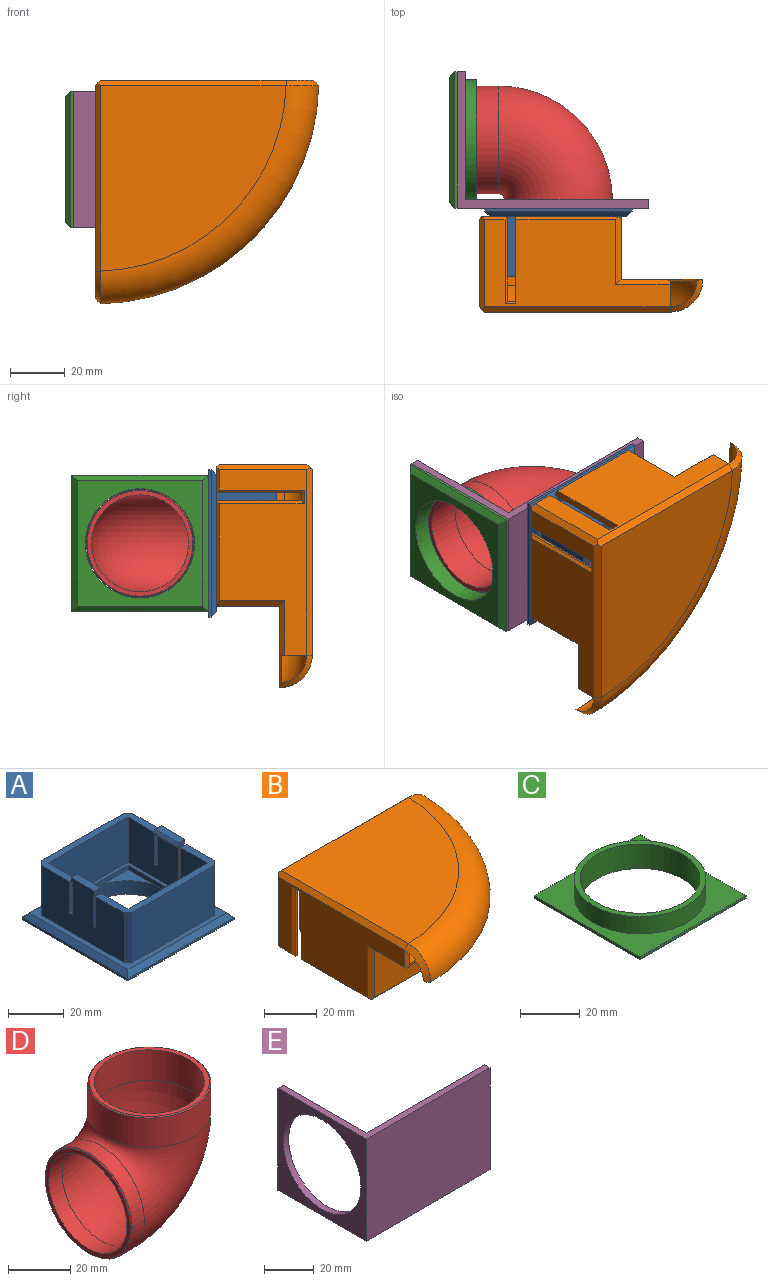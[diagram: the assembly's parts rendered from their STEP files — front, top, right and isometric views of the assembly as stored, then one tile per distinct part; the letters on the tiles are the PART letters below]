
ASSEMBLY  parts=5 mates=4
PART A: 68 faces, bbox 54x54x30 mm
  f0: cylinder r=22mm len=44mm, axis (0,0,1), area 414.7mm2, adj f53,f55
  f1: plane 12.49x1mm, normal (0,0,-1), area 8.4mm2, adj f16,f52
  f2: plane 12.49x1mm, normal (0,0,-1), area 8.4mm2, adj f15,f52
  f3: plane 12.49x1mm, normal (0,0,-1), area 8.4mm2, adj f18,f52
  f4: plane 12.49x1mm, normal (0,0,-1), area 8.4mm2, adj f17,f52
  f5: plane 40.5x20.5mm, normal (1,0,0), area 782.4mm2, adj f8,f9,f13,f14,f19,f20,f21,f34
  f6: plane 40.5x20.5mm, normal (-1,0,0), area 782.4mm2, adj f8,f9,f13,f14,f19,f23,f24,f26
  f7: plane 42x24mm, normal (1,0,0), area 914.4mm2, adj f8,f9,f23,f24,f25,f26,f27,f28
  f8: plane 46x16.4mm, normal (0,0,1), area 197.6mm2, adj f5,f6,f7,f11,f12,f14,f33,f34
  f9: plane 46x16.4mm, normal (0,0,1), area 197.6mm2, adj f5,f6,f7,f10,f11,f13,f29,f39
  f10: plane 42x22mm, normal (0,1,0), area 924mm2, adj f9,f54,f61,f62
  f11: plane 42x24mm, normal (-1,0,0), area 914.4mm2, adj f8,f9,f20,f21,f22,f34,f35,f36
  f12: plane 42x22mm, normal (0,-1,0), area 924mm2, adj f8,f54,f60,f63
  f13: plane 40.5x20mm, normal (0,-1,0), area 810mm2, adj f5,f6,f9,f19
  f14: plane 40.5x20mm, normal (0,1,0), area 810mm2, adj f5,f6,f8,f19
  f15: plane 38x2mm, normal (1,0,0), area 76mm2, adj f2,f16,f18,f19,f48,f49
  f16: plane 38x2mm, normal (0,-1,0), area 76mm2, adj f1,f15,f17,f19,f48,f50
  f17: plane 38x2mm, normal (-1,0,0), area 76mm2, adj f4,f16,f18,f19,f50,f51
  f18: plane 38x2mm, normal (0,1,0), area 76mm2, adj f3,f15,f17,f19,f49,f51
  f19: plane 40.5x40.5mm, normal (0,0,1), area 196.3mm2, adj f5,f6,f13,f14,f15,f16,f17,f18
  f20: plane 4.25x2mm, normal (0,-1,0), area 7.3mm2, adj f5,f11,f22,f35,f42,f43,f44
  f21: plane 4.25x2mm, normal (0,1,0), area 7.3mm2, adj f5,f11,f22,f38,f42,f43,f44
  f22: plane 12x3.25mm, normal (0,0,1), area 39mm2, adj f11,f20,f21,f44
  f23: plane 4.25x2mm, normal (0,-1,0), area 7.3mm2, adj f6,f7,f25,f30,f45,f46,f47
  f24: plane 4.25x2mm, normal (0,1,0), area 7.3mm2, adj f6,f7,f25,f26,f45,f46,f47
  f25: plane 12x3.25mm, normal (0,0,1), area 39mm2, adj f7,f23,f24,f47
  f26: plane 2.75x0.6mm, normal (0,0,-1), area 1.6mm2, adj f6,f7,f24,f27
  f27: plane 14x2.75mm, normal (0,1,0), area 38.5mm2, adj f6,f7,f26,f28
  f28: plane 2.75x1.2mm, normal (0,0,1), area 3.3mm2, adj f6,f7,f27,f29
  f29: plane 14x2.75mm, normal (0,-1,0), area 38.5mm2, adj f6,f7,f9,f28
  f30: plane 2.75x0.6mm, normal (0,0,-1), area 1.6mm2, adj f6,f7,f23,f32
  f31: plane 2.75x1.2mm, normal (0,0,1), area 3.3mm2, adj f6,f7,f32,f33
  f32: plane 14x2.75mm, normal (0,-1,0), area 38.5mm2, adj f6,f7,f30,f31
  f33: plane 14x2.75mm, normal (0,1,0), area 38.5mm2, adj f6,f7,f8,f31
  f34: plane 14x2.75mm, normal (0,1,0), area 38.5mm2, adj f5,f8,f11,f37
  f35: plane 2.75x0.6mm, normal (0,0,-1), area 1.7mm2, adj f5,f11,f20,f36
  f36: plane 14x2.75mm, normal (0,-1,0), area 38.5mm2, adj f5,f11,f35,f37
  f37: plane 2.75x1.2mm, normal (0,0,1), area 3.3mm2, adj f5,f11,f34,f36
  f38: plane 2.75x0.6mm, normal (0,0,-1), area 1.7mm2, adj f5,f11,f21,f41
  f39: plane 14x2.75mm, normal (0,-1,0), area 38.5mm2, adj f5,f9,f11,f40
  f40: plane 2.75x1.2mm, normal (0,0,1), area 3.3mm2, adj f5,f11,f39,f41
  f41: plane 14x2.75mm, normal (0,1,0), area 38.5mm2, adj f5,f11,f38,f40
  f42: plane 12x1.5mm, normal (0,0,-1), area 18mm2, adj f5,f20,f21,f43
  f43: plane 12x0.5mm, normal (1,0,0), area 6mm2, adj f20,f21,f42,f44
  f44: plane 12x1mm, normal (0.71,0,0.71), area 17mm2, adj f20,f21,f22,f43
  f45: plane 12x1.5mm, normal (0,0,-1), area 18mm2, adj f6,f23,f24,f46
  f46: plane 12x0.5mm, normal (-1,0,0), area 6mm2, adj f23,f24,f45,f47
  f47: plane 12x1mm, normal (-0.71,0,0.71), area 17mm2, adj f23,f24,f25,f46
  f48: plane 12.76x12.76mm, normal (0,0,1), area 55.2mm2, adj f15,f16,f52
  f49: plane 12.76x12.76mm, normal (0,0,1), area 55.2mm2, adj f15,f18,f52
  f50: plane 12.76x12.76mm, normal (0,0,1), area 55.2mm2, adj f16,f17,f52
  f51: plane 12.76x12.76mm, normal (0,0,1), area 55.2mm2, adj f17,f18,f52
  f52: cylinder r=20mm len=40mm, axis (0,0,1), area 754mm2, adj f1,f2,f3,f4,f48,f49,f50,f51
  f53: plane 44x44mm, normal (0,0,-1), area 263.9mm2, adj f0,f52
  f54: plane 50x50mm, normal (0,0,1), area 392mm2, adj f7,f10,f11,f12,f60,f61,f62,f63
  f55: plane 54x54mm, normal (0,0,-1), area 1395.5mm2, adj f0,f56,f57,f58,f59
  f56: plane 54x1mm, normal (0,1,0), area 54mm2, adj f55,f57,f59,f67
  f57: plane 54x1mm, normal (1,0,0), area 54mm2, adj f55,f56,f58,f66
  f58: plane 54x1mm, normal (0,-1,0), area 54mm2, adj f55,f57,f59,f64
  f59: plane 54x1mm, normal (-1,0,0), area 54mm2, adj f55,f56,f58,f65
  f60: plane 22x2mm, normal (-0.71,-0.71,0), area 62.2mm2, adj f8,f11,f12,f54
  f61: plane 22x2mm, normal (-0.71,0.71,0), area 62.2mm2, adj f9,f10,f11,f54
  f62: plane 22x2mm, normal (0.71,0.71,0), area 62.2mm2, adj f7,f9,f10,f54
  f63: plane 22x2mm, normal (0.71,-0.71,0), area 62.2mm2, adj f7,f8,f12,f54
  f64: plane 54x2mm, normal (0,-0.71,0.71), area 147.1mm2, adj f54,f58,f65,f66
  f65: plane 54x2mm, normal (-0.71,0,0.71), area 147.1mm2, adj f54,f59,f64,f67
  f66: plane 54x2mm, normal (0.71,0,0.71), area 147.1mm2, adj f54,f57,f64,f67
  f67: plane 54x2mm, normal (0,0.71,0.71), area 147.1mm2, adj f54,f56,f65,f66
PART B: 59 faces, bbox 88.7x88.7x35 mm
  f0: plane 65.2x33mm, normal (1,0,0), area 1424.1mm2, adj f1,f3,f11,f12,f16,f30,f33,f42
  f1: plane 50x50mm, normal (0,0,-1), area 302.6mm2, adj f0,f8,f9,f10,f31,f32,f33,f35
  f2: cylinder r=70mm len=46.86mm, axis (0,0,1), area 72.8mm2, adj f5,f6,f8,f11,f17,f29,f54
  f3: cylinder r=70mm len=46.86mm, axis (0,0,1), area 72.8mm2, adj f0,f4,f7,f11,f17,f28,f58
  f4: plane 48.01x24.01mm, normal (0,-1,0), area 1063mm2, adj f3,f11,f14,f20,f22,f57,f58
  f5: plane 48.01x24.01mm, normal (1,0,0), area 1063mm2, adj f2,f11,f13,f20,f21,f54,f56
  f6: plane 68x32mm, normal (0,1,0), area 1572mm2, adj f2,f21,f23,f26,f27,f29,f35,f45
  f7: plane 68x32mm, normal (-1,0,0), area 1541mm2, adj f3,f22,f23,f24,f25,f28,f48,f49
  f8: plane 65.2x33mm, normal (0,-1,0), area 1456.1mm2, adj f1,f2,f11,f12,f16,f30,f31,f35
  f9: plane 42.5x25mm, normal (-1,0,0), area 1062.5mm2, adj f1,f11,f31,f32
  f10: plane 42.5x25mm, normal (0,1,0), area 1062.5mm2, adj f1,f11,f32,f33
  f11: plane 67.2x67.2mm, normal (0,0,1), area 1325.6mm2, adj f0,f2,f3,f4,f5,f8,f9,f10
  f12: plane 9.5x9.5mm, normal (0,0,-1), area 31.2mm2, adj f0,f8,f30,f36,f39,f40,f43,f45
  f13: plane 43.35x16.97mm, normal (0,0,-1), area 494.2mm2, adj f5,f29,f54
  f14: plane 43.35x16.97mm, normal (0,0,-1), area 494.2mm2, adj f4,f28,f58
  f15: plane 67.97x67.97mm, normal (0,0,1), area 3572.3mm2, adj f19,f25,f26
  f16: plane 67.2x67.2mm, normal (0,0,-1), area 3469.1mm2, adj f0,f8,f17,f30
  f17: torus R=70mm, axis (0,0,-1), area 1769.5mm2, adj f2,f3,f16,f24,f27,f53
  f18: plane 80.98x80.98mm, normal (0,0,-1), area 130.5mm2, adj f19,f24,f27,f53
  f19: torus R=70mm, axis (0,0,-1), area 2220.5mm2, adj f15,f18,f24,f27
  f20: plane 25x2mm, normal (0.71,-0.71,0), area 69.3mm2, adj f4,f5,f11,f56,f57
  f21: plane 25x2mm, normal (0.71,0.71,0), area 66.5mm2, adj f5,f6,f29,f55,f56
  f22: plane 25x2mm, normal (-0.71,-0.71,0), area 66.5mm2, adj f4,f7,f28,f49,f57
  f23: plane 34x2mm, normal (-0.71,0.71,0), area 93.3mm2, adj f6,f7,f25,f26,f45,f48
  f24: bspline ~12x12mm, area 48.3mm2, adj f7,f17,f18,f19,f25,f53
  f25: plane 68.97x2mm, normal (-0.71,0,0.71), area 193.7mm2, adj f7,f15,f23,f24,f26
  f26: plane 68.97x2mm, normal (0,0.71,0.71), area 193.7mm2, adj f6,f15,f23,f25,f27
  f27: bspline ~12x12mm, area 48.3mm2, adj f6,f17,f18,f19,f26,f53
  f28: plane 20.01x2.01mm, normal (-0.71,0,-0.71), area 53mm2, adj f3,f7,f14,f22,f58
  f29: plane 20.01x2.01mm, normal (0,0.71,-0.71), area 53mm2, adj f2,f6,f13,f21,f54
  f30: plane 33x2mm, normal (0.71,-0.71,0), area 93.3mm2, adj f0,f8,f12,f16
  f31: plane 25x2mm, normal (-0.71,-0.71,0), area 70.7mm2, adj f1,f8,f9,f11
  f32: plane 25x2mm, normal (-0.71,0.71,0), area 70.7mm2, adj f1,f9,f10,f11
  f33: plane 25x2mm, normal (0.71,0.71,0), area 70.7mm2, adj f0,f1,f10,f11
  f34: plane 3x0.75mm, normal (0,0,-1), area 2.3mm2, adj f35,f36,f41,f47
  f35: plane 32x2.75mm, normal (-1,0,0), area 85.8mm2, adj f1,f6,f8,f34,f41,f47,f55
  f36: plane 31x0.75mm, normal (1,0,0), area 23.3mm2, adj f12,f34,f40,f46
  f37: plane 31x0.75mm, normal (0,1,0), area 23.3mm2, adj f1,f38,f42,f51
  f38: plane 3x0.75mm, normal (0,0,-1), area 2.3mm2, adj f37,f39,f44,f52
  f39: plane 31x0.75mm, normal (0,-1,0), area 23.3mm2, adj f12,f38,f43,f50
  f40: plane 32x1mm, normal (0.71,-0.71,0), area 44.5mm2, adj f8,f12,f36,f41
  f41: plane 4x1mm, normal (0,-0.71,-0.71), area 4.9mm2, adj f8,f34,f35,f40
  f42: plane 32x1mm, normal (0.71,0.71,0), area 44.5mm2, adj f0,f1,f37,f44
  f43: plane 32x1mm, normal (0.71,-0.71,0), area 44.5mm2, adj f0,f12,f39,f44
  f44: plane 5x1mm, normal (0.71,0,-0.71), area 5.7mm2, adj f0,f38,f42,f43
  f45: plane 9.5x1mm, normal (0,0.71,-0.71), area 12mm2, adj f6,f12,f23,f46
  f46: plane 32x1mm, normal (0.71,0.71,0), area 43.8mm2, adj f6,f36,f45,f47
  f47: plane 4x1mm, normal (0,0.71,-0.71), area 4.9mm2, adj f6,f34,f35,f46
  f48: plane 9.5x1mm, normal (-0.71,0,-0.71), area 12mm2, adj f7,f12,f23,f50
  f49: plane 37.5x1mm, normal (-0.71,0,-0.71), area 51.6mm2, adj f1,f7,f22,f51
  f50: plane 32x1mm, normal (-0.71,-0.71,0), area 43.8mm2, adj f7,f39,f48,f52
  f51: plane 32x1mm, normal (-0.71,0.71,0), area 43.8mm2, adj f7,f37,f49,f52
  f52: plane 5x1mm, normal (-0.71,0,-0.71), area 5.7mm2, adj f7,f38,f50,f51
  f53: cone r=79.96mm half-angle=47.6deg, axis (0,0,-1), area 169mm2, adj f17,f18,f24,f27
  f54: cone r=70mm half-angle=45deg, axis (0,0,1), area 69.2mm2, adj f2,f5,f13,f29
  f55: plane 37.5x1mm, normal (0,0.71,-0.71), area 52.3mm2, adj f1,f6,f21,f35
  f56: plane 50x1mm, normal (0.71,0,-0.71), area 69.3mm2, adj f1,f5,f20,f21
  f57: plane 50x1mm, normal (0,-0.71,-0.71), area 69.3mm2, adj f1,f4,f20,f22
  f58: cone r=70mm half-angle=45deg, axis (0,0,1), area 69.2mm2, adj f3,f4,f14,f28
PART C: 13 faces, bbox 50x50x10 mm
  f0: plane 50x1mm, normal (0,1,0), area 50mm2, adj f1,f3,f4,f12
  f1: plane 50x1mm, normal (-1,0,0), area 50mm2, adj f0,f2,f4,f10
  f2: plane 50x1mm, normal (0,-1,0), area 50mm2, adj f1,f3,f4,f9
  f3: plane 50x1mm, normal (1,0,0), area 50mm2, adj f0,f2,f4,f11
  f4: plane 50x50mm, normal (0,0,1), area 979.5mm2, adj f0,f1,f2,f3,f7
  f5: plane 46x46mm, normal (0,0,-1), area 859.4mm2, adj f6,f9,f10,f11,f12
  f6: cylinder r=20mm len=40mm, axis (0,0,-1), area 1256.6mm2, adj f5,f8
  f7: cylinder r=22mm len=44mm, axis (0,0,-1), area 967.6mm2, adj f4,f8
  f8: plane 44x44mm, normal (0,0,1), area 263.9mm2, adj f6,f7
  f9: plane 50x2mm, normal (0,-0.71,-0.71), area 135.8mm2, adj f2,f5,f10,f11
  f10: plane 50x2mm, normal (-0.71,0,-0.71), area 135.8mm2, adj f1,f5,f9,f12
  f11: plane 50x2mm, normal (0.71,0,-0.71), area 135.8mm2, adj f3,f5,f9,f12
  f12: plane 50x2mm, normal (0,0.71,-0.71), area 135.8mm2, adj f0,f5,f10,f11
PART D: 10 faces, bbox 51.2x39.5x57.2 mm
  f0: torus R=22mm, axis (0,1,0), area 3854.1mm2, adj f2,f5
  f1: torus R=22mm, axis (0,1,0), area 4288.3mm2, adj f3,f6
  f2: cylinder r=17.75mm len=35.5mm, axis (0,0,-1), area 1338.3mm2, adj f0,f4
  f3: cylinder r=19.75mm len=39.5mm, axis (0,0,-1), area 1439.5mm2, adj f1,f9
  f4: plane 38.7x38.7mm, normal (0,0,1), area 186.5mm2, adj f2,f9
  f5: cylinder r=17.75mm len=35.5mm, axis (1,0,0), area 669.2mm2, adj f0,f7
  f6: cylinder r=19.75mm len=39.5mm, axis (1,0,0), area 694.9mm2, adj f1,f8
  f7: plane 38.7x38.7mm, normal (-1,0,0), area 186.5mm2, adj f5,f8
  f8: cone r=19.35mm half-angle=45deg, axis (1,0,0), area 69.5mm2, adj f6,f7
  f9: cone r=19.75mm half-angle=45deg, axis (0,0,-1), area 69.5mm2, adj f3,f4
PART E: 9 faces, bbox 70x50x50 mm
  f0: plane 50x50mm, normal (-1,0,0), area 979.5mm2, adj f1,f5,f6,f7,f8
  f1: plane 70x50mm, normal (0,-1,0), area 3500mm2, adj f0,f2,f6,f7
  f2: plane 50x3mm, normal (1,0,0), area 150mm2, adj f1,f3,f6,f7
  f3: plane 67x50mm, normal (0,1,0), area 3350mm2, adj f2,f4,f6,f7
  f4: plane 50x47mm, normal (1,0,0), area 829.5mm2, adj f3,f5,f6,f7,f8
  f5: plane 50x3mm, normal (0,1,0), area 150mm2, adj f0,f4,f6,f7
  f6: plane 70x50mm, normal (0,0,1), area 351mm2, adj f0,f1,f2,f3,f4,f5
  f7: plane 70x50mm, normal (0,0,-1), area 351mm2, adj f0,f1,f2,f3,f4,f5
  f8: cylinder r=22mm len=44mm, axis (-1,0,0), area 414.7mm2, adj f0,f4
PLACE A rot(axis=(1,0,0),90deg) t=(-106.54,-77.9,20.8)mm
PLACE B rot(axis=(1,0,0),90deg) t=(-109.58,-77.9,23.83)mm
PLACE C rot(axis=(0,1,0),90deg) t=(-146.54,-49.8,20.8)mm
PLACE D rot(axis=(-0.58,-0.58,0.58),120deg) t=(-128.54,-49.8,20.8)mm
PLACE E t=(-140.54,-74.8,-4.2)mm
MATE fastened B.f1 <-> A.f0  axis (0,1,0) through (-106.54,-77.9,20.8)mm
MATE fastened A.f52 <-> D.f6  axis (0,-1,0) through (-106.54,-77.9,20.8)mm
MATE fastened C.f4 <-> E.f0  axis (1,0,0) through (-143.54,-24.8,20.8)mm
MATE fastened D.f3 <-> E.f8  axis (-1,0,0) through (-140.54,-49.8,20.8)mm
